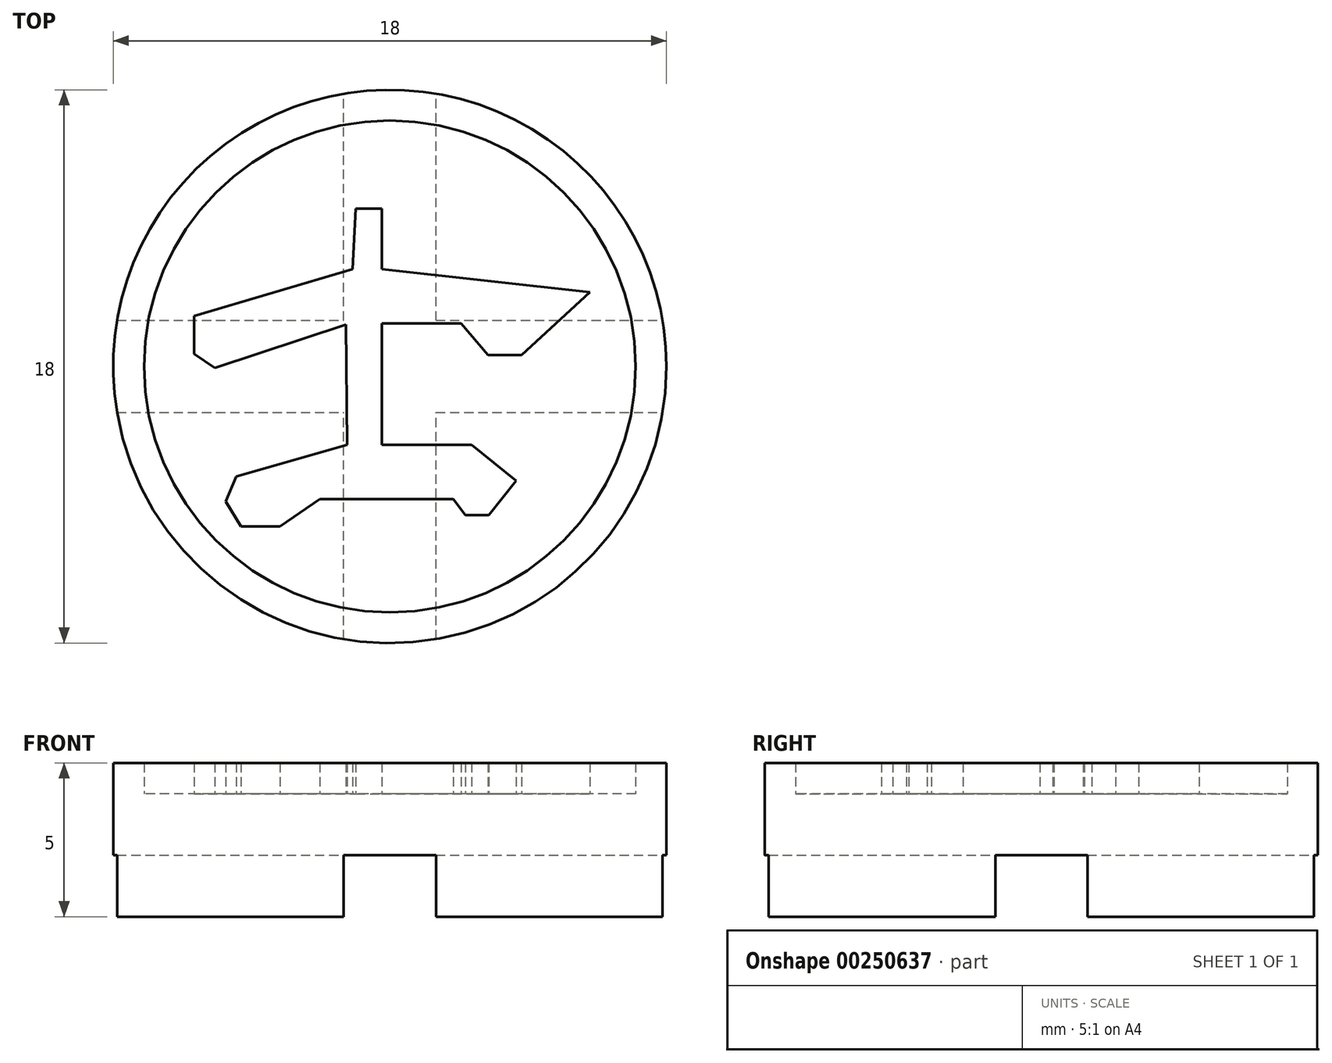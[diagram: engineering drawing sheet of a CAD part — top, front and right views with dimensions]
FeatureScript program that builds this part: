
annotation { "Feature Type Name" : "Feature", "Feature Type Description" : "" }
export const myFeature = defineFeature(function(context is Context, id is Id, definition is map)
    precondition{}
    {
        {
            var Q0;
            Q0=qCreatedBy(makeId("Top.planeOp"),FACE);
            var sketch = newSketch(context, id + "F0", { "sketchPlane" : qUnion([Q0])});
            skCircle(sketch, "E0", {"center": v(-31.33, 19.76) * mm, "radius": 9 * mm});
            skSolve(sketch);
        }
        {
            var Q0;
            Q0 = qSketchRegion(id + "F0", true);
            extrude(context, id + "F1", {"entities" : qUnion([Q0]), "depth" : 4 * mm});
        }
        {
            var Q0;
            Q0=makeQuery(id+"F1.opExtrude","CAP_FACE",FACE,{"disambiguationData":[OSD([sQuery(id+"F0.wireOp",EDGE,"E0")])],"isStart":false});
            var sketch = newSketch(context, id + "F2", { "sketchPlane" : qUnion([Q0])});
            skCircle(sketch, "E1", {"center": v(-31.33, 19.76) * mm, "radius": 8 * mm});
            skCircle(sketch, "E2", {"center": v(-31.33, 19.76) * mm, "radius": 9 * mm});
            skLineSegment(sketch, "E3", {"start": v(-32.44, 24.89) * mm, "end": v(-31.59, 24.89) * mm});
            skLineSegment(sketch, "E4", {"start": v(-31.59, 24.89) * mm, "end": v(-31.59, 22.92) * mm});
            skLineSegment(sketch, "E5", {"start": v(-31.59, 22.92) * mm, "end": v(-24.82, 22.18) * mm});
            skLineSegment(sketch, "E6", {"start": v(-24.82, 22.18) * mm, "end": v(-27.04, 20.13) * mm});
            skLineSegment(sketch, "E7", {"start": v(-27.04, 20.13) * mm, "end": v(-28.14, 20.13) * mm});
            skLineSegment(sketch, "E8", {"start": v(-28.14, 20.13) * mm, "end": v(-29.02, 21.16) * mm});
            skLineSegment(sketch, "E9", {"start": v(-29.02, 21.16) * mm, "end": v(-31.59, 21.16) * mm});
            skLineSegment(sketch, "E10", {"start": v(-31.59, 21.16) * mm, "end": v(-31.59, 17.2) * mm});
            skLineSegment(sketch, "E11", {"start": v(-31.59, 17.2) * mm, "end": v(-28.67, 17.2) * mm});
            skLineSegment(sketch, "E12", {"start": v(-28.67, 17.2) * mm, "end": v(-27.22, 16.04) * mm});
            skLineSegment(sketch, "E13", {"start": v(-27.22, 16.04) * mm, "end": v(-28.12, 14.92) * mm});
            skLineSegment(sketch, "E14", {"start": v(-28.12, 14.92) * mm, "end": v(-28.88, 14.92) * mm});
            skLineSegment(sketch, "E15", {"start": v(-28.88, 14.92) * mm, "end": v(-29.27, 15.44) * mm});
            skLineSegment(sketch, "E16", {"start": v(-29.27, 15.44) * mm, "end": v(-33.6, 15.44) * mm});
            skLineSegment(sketch, "E17", {"start": v(-33.6, 15.44) * mm, "end": v(-34.91, 14.56) * mm});
            skLineSegment(sketch, "E18", {"start": v(-34.91, 14.56) * mm, "end": v(-36.18, 14.56) * mm});
            skLineSegment(sketch, "E19", {"start": v(-36.18, 14.56) * mm, "end": v(-36.67, 15.37) * mm});
            skLineSegment(sketch, "E20", {"start": v(-36.67, 15.37) * mm, "end": v(-36.32, 16.18) * mm});
            skLineSegment(sketch, "E21", {"start": v(-36.32, 16.18) * mm, "end": v(-32.72, 17.2) * mm});
            skLineSegment(sketch, "E22", {"start": v(-32.72, 17.2) * mm, "end": v(-32.76, 21.12) * mm});
            skLineSegment(sketch, "E23", {"start": v(-32.76, 21.12) * mm, "end": v(-37.03, 19.7) * mm});
            skLineSegment(sketch, "E24", {"start": v(-37.03, 19.7) * mm, "end": v(-37.7, 20.17) * mm});
            skLineSegment(sketch, "E25", {"start": v(-37.7, 20.17) * mm, "end": v(-37.7, 21.4) * mm});
            skLineSegment(sketch, "E26", {"start": v(-37.7, 21.4) * mm, "end": v(-32.55, 22.92) * mm});
            skLineSegment(sketch, "E27", {"start": v(-32.55, 22.92) * mm, "end": v(-32.44, 24.89) * mm});
            skSolve(sketch);
        }
        {
            var Q0;
            Q0=makeQuery(id+"F1.opExtrude","CAP_FACE",FACE,{"disambiguationData":[OSD([sQuery(id+"F0.wireOp",EDGE,"E0")])],"isStart":true});
            var sketch = newSketch(context, id + "F3", { "sketchPlane" : qUnion([Q0])});
            skLineSegment(sketch, "E28", {"start": v(-31.33, -19.76) * mm, "end": v(-22.33, -19.76) * mm, "construction": true});
            skLineSegment(sketch, "E29", {"start": v(-31.33, -19.76) * mm, "end": v(-31.33, -10.76) * mm, "construction": true});
            skLineSegment(sketch, "E30", {"start": v(-31.33, -19.76) * mm, "end": v(-40.33, -19.76) * mm, "construction": true});
            skLineSegment(sketch, "E31", {"start": v(-31.33, -19.76) * mm, "end": v(-31.33, -28.76) * mm, "construction": true});
            skLineSegment(sketch, "E32.bottom", {"start": v(-40.33, -28.76) * mm, "end": v(-22.33, -28.76) * mm});
            skLineSegment(sketch, "E32.top", {"start": v(-40.33, -10.76) * mm, "end": v(-22.33, -10.76) * mm});
            skLineSegment(sketch, "E32.left", {"start": v(-22.33, -10.76) * mm, "end": v(-22.33, -28.76) * mm});
            skLineSegment(sketch, "E32.right", {"start": v(-40.33, -10.76) * mm, "end": v(-40.33, -28.76) * mm});
            skPoint(sketch, "E33", {"position": v(-31.33, -28.76) * mm});
            skPoint(sketch, "E34", {"position": v(-40.33, -19.76) * mm});
            skPoint(sketch, "E35", {"position": v(-22.33, -19.76) * mm});
            skPoint(sketch, "E36", {"position": v(-31.33, -10.76) * mm});
            skLineSegment(sketch, "E37.bottom", {"start": v(-32.83, -10.76) * mm, "end": v(-29.83, -10.76) * mm});
            skLineSegment(sketch, "E37.top", {"start": v(-32.83, -28.76) * mm, "end": v(-29.83, -28.76) * mm});
            skLineSegment(sketch, "E37.left", {"start": v(-32.83, -10.76) * mm, "end": v(-32.83, -28.76) * mm});
            skLineSegment(sketch, "E37.right", {"start": v(-29.83, -10.76) * mm, "end": v(-29.83, -28.76) * mm});
            skLineSegment(sketch, "E38.bottom", {"start": v(-40.33, -18.26) * mm, "end": v(-22.33, -18.26) * mm});
            skLineSegment(sketch, "E38.top", {"start": v(-40.33, -21.26) * mm, "end": v(-22.33, -21.26) * mm});
            skLineSegment(sketch, "E38.left", {"start": v(-40.33, -18.26) * mm, "end": v(-40.33, -21.26) * mm});
            skLineSegment(sketch, "E38.right", {"start": v(-22.33, -18.26) * mm, "end": v(-22.33, -21.26) * mm});
            skSolve(sketch);
        }
        {
            var Q0;
            {var subQ1=sQuery(id+"F3.wireOp",EDGE,"E37.bottom");var subQ3=makeQuery(id+"F1.opExtrude","CAP_EDGE",EDGE,{"disambiguationData":[OSD([sQuery(id+"F0.wireOp",EDGE,"E0")])],"isStart":true});var subQ4=makeQuery(id+"F3.imprint","INTERSECT",VERTEX,{"derivedFrom":[subQ3,subQ1]});Q0=makeQuery(id+"F3.imprint","IMPRINT",FACE,{"disambiguationData":[TD([[makeQuery(id+"F3.imprint","IMPRINT",EDGE,{"disambiguationData":[TD([[subQ4,1.0]])],"derivedFrom":subQ3}),1.0]])]});}
            var Q1;
            {var subQ1=sQuery(id+"F3.wireOp",EDGE,"E37.bottom");var subQ3=makeQuery(id+"F1.opExtrude","CAP_EDGE",EDGE,{"disambiguationData":[OSD([sQuery(id+"F0.wireOp",EDGE,"E0")])],"isStart":true});var subQ4=makeQuery(id+"F3.imprint","INTERSECT",VERTEX,{"derivedFrom":[subQ3,subQ1]});Q1=makeQuery(id+"F3.imprint","IMPRINT",FACE,{"disambiguationData":[TD([[makeQuery(id+"F3.imprint","IMPRINT",EDGE,{"disambiguationData":[TD([[subQ4,-1.0]])],"derivedFrom":subQ3}),1.0]])]});}
            var Q2;
            {var subQ1=sQuery(id+"F3.wireOp",EDGE,"E37.top");var subQ3=makeQuery(id+"F1.opExtrude","CAP_EDGE",EDGE,{"disambiguationData":[OSD([sQuery(id+"F0.wireOp",EDGE,"E0")])],"isStart":true});var subQ4=makeQuery(id+"F3.imprint","INTERSECT",VERTEX,{"derivedFrom":[subQ3,subQ1]});Q2=makeQuery(id+"F3.imprint","IMPRINT",FACE,{"disambiguationData":[TD([[makeQuery(id+"F3.imprint","IMPRINT",EDGE,{"disambiguationData":[TD([[subQ4,-1.0]])],"derivedFrom":subQ3}),1.0]])]});}
            var Q3;
            {var subQ1=sQuery(id+"F3.wireOp",EDGE,"E37.top");var subQ3=makeQuery(id+"F1.opExtrude","CAP_EDGE",EDGE,{"disambiguationData":[OSD([sQuery(id+"F0.wireOp",EDGE,"E0")])],"isStart":true});var subQ4=makeQuery(id+"F3.imprint","INTERSECT",VERTEX,{"derivedFrom":[subQ3,subQ1]});Q3=makeQuery(id+"F3.imprint","IMPRINT",FACE,{"disambiguationData":[TD([[makeQuery(id+"F3.imprint","IMPRINT",EDGE,{"disambiguationData":[TD([[subQ4,1.0]])],"derivedFrom":subQ3}),1.0]])]});}
            var Q4;
            {var subQ0=sQuery(id+"F3.wireOp",EDGE,"E38.left");var subQ3=makeQuery(id+"F1.opExtrude","CAP_EDGE",EDGE,{"disambiguationData":[OSD([sQuery(id+"F0.wireOp",EDGE,"E0")])],"isStart":true});var subQ5=makeQuery(id+"F3.imprint","INTERSECT",VERTEX,{"derivedFrom":[subQ3,subQ0]});Q4=makeQuery(id+"F3.imprint","IMPRINT",FACE,{"disambiguationData":[TD([[makeQuery(id+"F3.imprint","IMPRINT",EDGE,{"disambiguationData":[TD([[subQ5,-1.0]])],"derivedFrom":subQ3}),1.0]])]});}
            var Q5;
            {var subQ0=sQuery(id+"F3.wireOp",EDGE,"E38.right");var subQ3=makeQuery(id+"F1.opExtrude","CAP_EDGE",EDGE,{"disambiguationData":[OSD([sQuery(id+"F0.wireOp",EDGE,"E0")])],"isStart":true});var subQ5=makeQuery(id+"F3.imprint","INTERSECT",VERTEX,{"derivedFrom":[subQ3,subQ0]});Q5=makeQuery(id+"F3.imprint","IMPRINT",FACE,{"disambiguationData":[TD([[makeQuery(id+"F3.imprint","IMPRINT",EDGE,{"disambiguationData":[TD([[subQ5,1.0]])],"derivedFrom":subQ3}),1.0]])]});}
            var Q6;
            {var subQ0=sQuery(id+"F3.wireOp",EDGE,"E38.left");var subQ3=makeQuery(id+"F1.opExtrude","CAP_EDGE",EDGE,{"disambiguationData":[OSD([sQuery(id+"F0.wireOp",EDGE,"E0")])],"isStart":true});var subQ5=makeQuery(id+"F3.imprint","INTERSECT",VERTEX,{"derivedFrom":[subQ3,subQ0]});Q6=makeQuery(id+"F3.imprint","IMPRINT",FACE,{"disambiguationData":[TD([[makeQuery(id+"F3.imprint","IMPRINT",EDGE,{"disambiguationData":[TD([[subQ5,1.0]])],"derivedFrom":subQ3}),1.0]])]});}
            var Q7;
            {var subQ0=sQuery(id+"F3.wireOp",EDGE,"E38.right");var subQ3=makeQuery(id+"F1.opExtrude","CAP_EDGE",EDGE,{"disambiguationData":[OSD([sQuery(id+"F0.wireOp",EDGE,"E0")])],"isStart":true});var subQ5=makeQuery(id+"F3.imprint","INTERSECT",VERTEX,{"derivedFrom":[subQ3,subQ0]});Q7=makeQuery(id+"F3.imprint","IMPRINT",FACE,{"disambiguationData":[TD([[makeQuery(id+"F3.imprint","IMPRINT",EDGE,{"disambiguationData":[TD([[subQ5,-1.0]])],"derivedFrom":subQ3}),1.0]])]});}
            var Q8;
            {var subQ3=makeQuery(id+"F1.opExtrude","CAP_EDGE",EDGE,{"disambiguationData":[OSD([sQuery(id+"F0.wireOp",EDGE,"E0")])],"isStart":true});var subQ5=sQuery(id+"F3.wireOp",EDGE,"E37.left");var subQ8=makeQuery(id+"F3.imprint","INTERSECT",VERTEX,{"disambiguationData":[OD(1.0)],"derivedFrom":[subQ3,subQ5]});Q8=makeQuery(id+"F3.imprint","IMPRINT",FACE,{"disambiguationData":[TD([[makeQuery(id+"F3.imprint","IMPRINT",EDGE,{"disambiguationData":[TD([[subQ8,-1.0]])],"derivedFrom":subQ3}),1.0]])]});}
            var Q9;
            {var subQ3=makeQuery(id+"F1.opExtrude","CAP_EDGE",EDGE,{"disambiguationData":[OSD([sQuery(id+"F0.wireOp",EDGE,"E0")])],"isStart":true});var subQ5=sQuery(id+"F3.wireOp",EDGE,"E37.right");var subQ8=makeQuery(id+"F3.imprint","INTERSECT",VERTEX,{"disambiguationData":[OD(1.0)],"derivedFrom":[subQ3,subQ5]});Q9=makeQuery(id+"F3.imprint","IMPRINT",FACE,{"disambiguationData":[TD([[makeQuery(id+"F3.imprint","IMPRINT",EDGE,{"disambiguationData":[TD([[subQ8,1.0]])],"derivedFrom":subQ3}),1.0]])]});}
            var Q10;
            {var subQ3=makeQuery(id+"F1.opExtrude","CAP_EDGE",EDGE,{"disambiguationData":[OSD([sQuery(id+"F0.wireOp",EDGE,"E0")])],"isStart":true});var subQ5=sQuery(id+"F3.wireOp",EDGE,"E37.left");var subQ8=makeQuery(id+"F3.imprint","INTERSECT",VERTEX,{"disambiguationData":[OD(0.0)],"derivedFrom":[subQ3,subQ5]});Q10=makeQuery(id+"F3.imprint","IMPRINT",FACE,{"disambiguationData":[TD([[makeQuery(id+"F3.imprint","IMPRINT",EDGE,{"disambiguationData":[TD([[subQ8,1.0]])],"derivedFrom":subQ3}),1.0]])]});}
            var Q11;
            {var subQ3=makeQuery(id+"F1.opExtrude","CAP_EDGE",EDGE,{"disambiguationData":[OSD([sQuery(id+"F0.wireOp",EDGE,"E0")])],"isStart":true});var subQ5=sQuery(id+"F3.wireOp",EDGE,"E37.right");var subQ8=makeQuery(id+"F3.imprint","INTERSECT",VERTEX,{"disambiguationData":[OD(0.0)],"derivedFrom":[subQ3,subQ5]});Q11=makeQuery(id+"F3.imprint","IMPRINT",FACE,{"disambiguationData":[TD([[makeQuery(id+"F3.imprint","IMPRINT",EDGE,{"disambiguationData":[TD([[subQ8,-1.0]])],"derivedFrom":subQ3}),1.0]])]});}
            var Q12;
            {var subQ2=sQuery(id+"F3.wireOp",EDGE,"E37.left");var subQ4=sQuery(id+"F3.wireOp",EDGE,"E38.bottom");var subQ8=makeQuery(id+"F3.imprint","INTERSECT",VERTEX,{"derivedFrom":[subQ2,subQ4]});Q12=makeQuery(id+"F3.imprint","IMPRINT",FACE,{"disambiguationData":[TD([[makeQuery(id+"F3.imprint","IMPRINT",EDGE,{"disambiguationData":[TD([[subQ8,1.0]])],"derivedFrom":subQ2}),1.0]])]});}
            var Q13;
            {var subQ1=sQuery(id+"F3.wireOp",EDGE,"E37.left");var subQ5=sQuery(id+"F3.wireOp",EDGE,"E38.bottom");var subQ6=makeQuery(id+"F3.imprint","INTERSECT",VERTEX,{"derivedFrom":[subQ1,subQ5]});Q13=makeQuery(id+"F3.imprint","IMPRINT",FACE,{"disambiguationData":[TD([[makeQuery(id+"F3.imprint","IMPRINT",EDGE,{"disambiguationData":[TD([[subQ6,-1.0]])],"derivedFrom":subQ1}),-1.0]])]});}
            var Q14;
            {var subQ0=sQuery(id+"F3.wireOp",EDGE,"E38.top");var subQ1=sQuery(id+"F3.wireOp",EDGE,"E37.left");var subQ2=makeQuery(id+"F3.imprint","INTERSECT",VERTEX,{"derivedFrom":[subQ1,subQ0]});Q14=makeQuery(id+"F3.imprint","IMPRINT",FACE,{"disambiguationData":[TD([[makeQuery(id+"F3.imprint","IMPRINT",EDGE,{"disambiguationData":[TD([[subQ2,-1.0]])],"derivedFrom":subQ1}),1.0]])]});}
            var Q15;
            {var subQ2=sQuery(id+"F3.wireOp",EDGE,"E38.bottom");var subQ5=sQuery(id+"F3.wireOp",EDGE,"E37.right");var subQ8=makeQuery(id+"F3.imprint","INTERSECT",VERTEX,{"derivedFrom":[subQ5,subQ2]});Q15=makeQuery(id+"F3.imprint","IMPRINT",FACE,{"disambiguationData":[TD([[makeQuery(id+"F3.imprint","IMPRINT",EDGE,{"disambiguationData":[TD([[subQ8,-1.0]])],"derivedFrom":subQ5}),1.0]])]});}
            var Q16;
            {var subQ0=sQuery(id+"F3.wireOp",EDGE,"E38.bottom");var subQ1=sQuery(id+"F3.wireOp",EDGE,"E37.left");var subQ2=makeQuery(id+"F3.imprint","INTERSECT",VERTEX,{"derivedFrom":[subQ1,subQ0]});Q16=makeQuery(id+"F3.imprint","IMPRINT",FACE,{"disambiguationData":[TD([[makeQuery(id+"F3.imprint","IMPRINT",EDGE,{"disambiguationData":[TD([[subQ2,-1.0]])],"derivedFrom":subQ1}),1.0]])]});}
            extrude(context, id + "F4", {"entities" : qUnion([Q0, Q1, Q2, Q3, Q4, Q5, Q6, Q7, Q8, Q9, Q10, Q11, Q12, Q13, Q14, Q15, Q16]), "operationType" : NewBodyOperationType.REMOVE, "oppositeDirection" : true, "depth" : 2 * mm});
        }
        {
            var Q0;
            Q0 = qSketchRegion(id + "F2", true);
            var Q1;
            Q1=makeQuery(id+"F2.imprint","IMPRINT",FACE,{"disambiguationData":[TD([[makeQuery(id+"F2.imprint","IMPRINT",EDGE,{"derivedFrom":sQuery(id+"F2.wireOp",EDGE,"E3")}),-1.0]])]});
            extrude(context, id + "F5", {"entities" : qUnion([Q0, Q1]), "operationType" : NewBodyOperationType.ADD, "depth" : 1 * mm});
        }
    });
